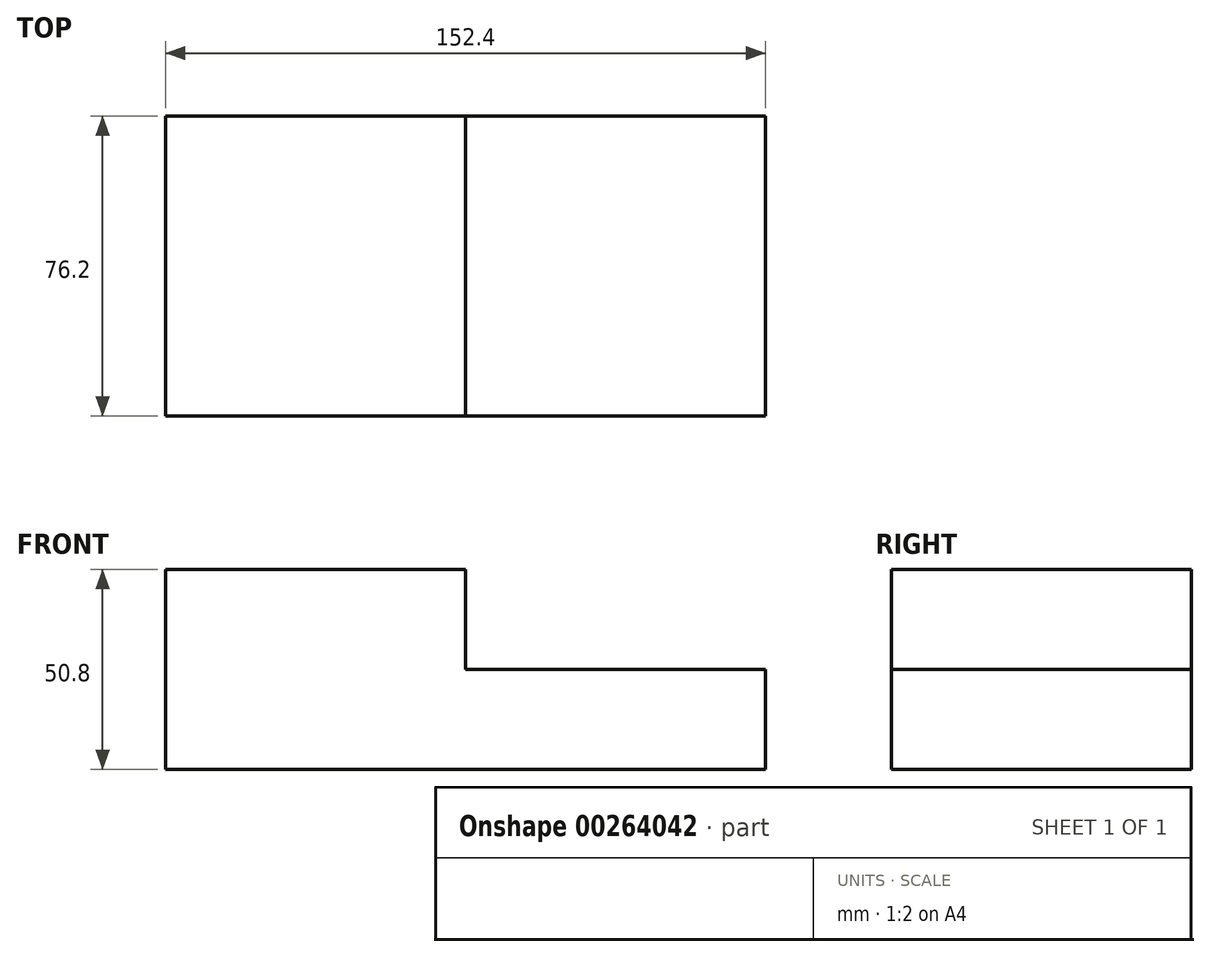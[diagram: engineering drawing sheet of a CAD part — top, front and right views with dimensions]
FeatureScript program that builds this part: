
annotation { "Feature Type Name" : "Feature", "Feature Type Description" : "" }
export const myFeature = defineFeature(function(context is Context, id is Id, definition is map)
    precondition{}
    {
        {
            var Q0;
            Q0=qCreatedBy(makeId("Front.planeOp"),FACE);
            var sketch = newSketch(context, id + "F0", { "sketchPlane" : qUnion([Q0])});
            skLineSegment(sketch, "E0.bottom", {"start": v(0, 0) * mm, "end": v(76.2, 0) * mm});
            skLineSegment(sketch, "E0.top", {"start": v(0, 25.4) * mm, "end": v(76.2, 25.4) * mm});
            skLineSegment(sketch, "E0.left", {"start": v(0, 0) * mm, "end": v(0, 25.4) * mm});
            skLineSegment(sketch, "E0.right", {"start": v(76.2, 0) * mm, "end": v(76.2, 25.4) * mm});
            skLineSegment(sketch, "E1.bottom", {"start": v(0, 0) * mm, "end": v(-76.2, 0) * mm});
            skLineSegment(sketch, "E1.top", {"start": v(0, 50.8) * mm, "end": v(-76.2, 50.8) * mm});
            skLineSegment(sketch, "E1.left", {"start": v(0, 0) * mm, "end": v(0, 50.8) * mm});
            skLineSegment(sketch, "E1.right", {"start": v(-76.2, 0) * mm, "end": v(-76.2, 50.8) * mm});
            skSolve(sketch);
        }
        {
            var Q0;
            {var subQ3=sQuery(id+"F0.wireOp",EDGE,"E1.bottom");Q0=makeQuery(id+"F0.imprint","IMPRINT",FACE,{"disambiguationData":[TD([[makeQuery(id+"F0.imprint","IMPRINT",EDGE,{"derivedFrom":subQ3}),-1.0]])]});}
            extrude(context, id + "F1", {"entities" : qUnion([Q0]), "depth" : 76.2 * mm});
        }
        {
            var Q0;
            Q0 = qSketchRegion(id + "F0", true);
            extrude(context, id + "F2", {"entities" : qUnion([Q0]), "operationType" : NewBodyOperationType.ADD, "depth" : 76.2 * mm});
        }
    });
